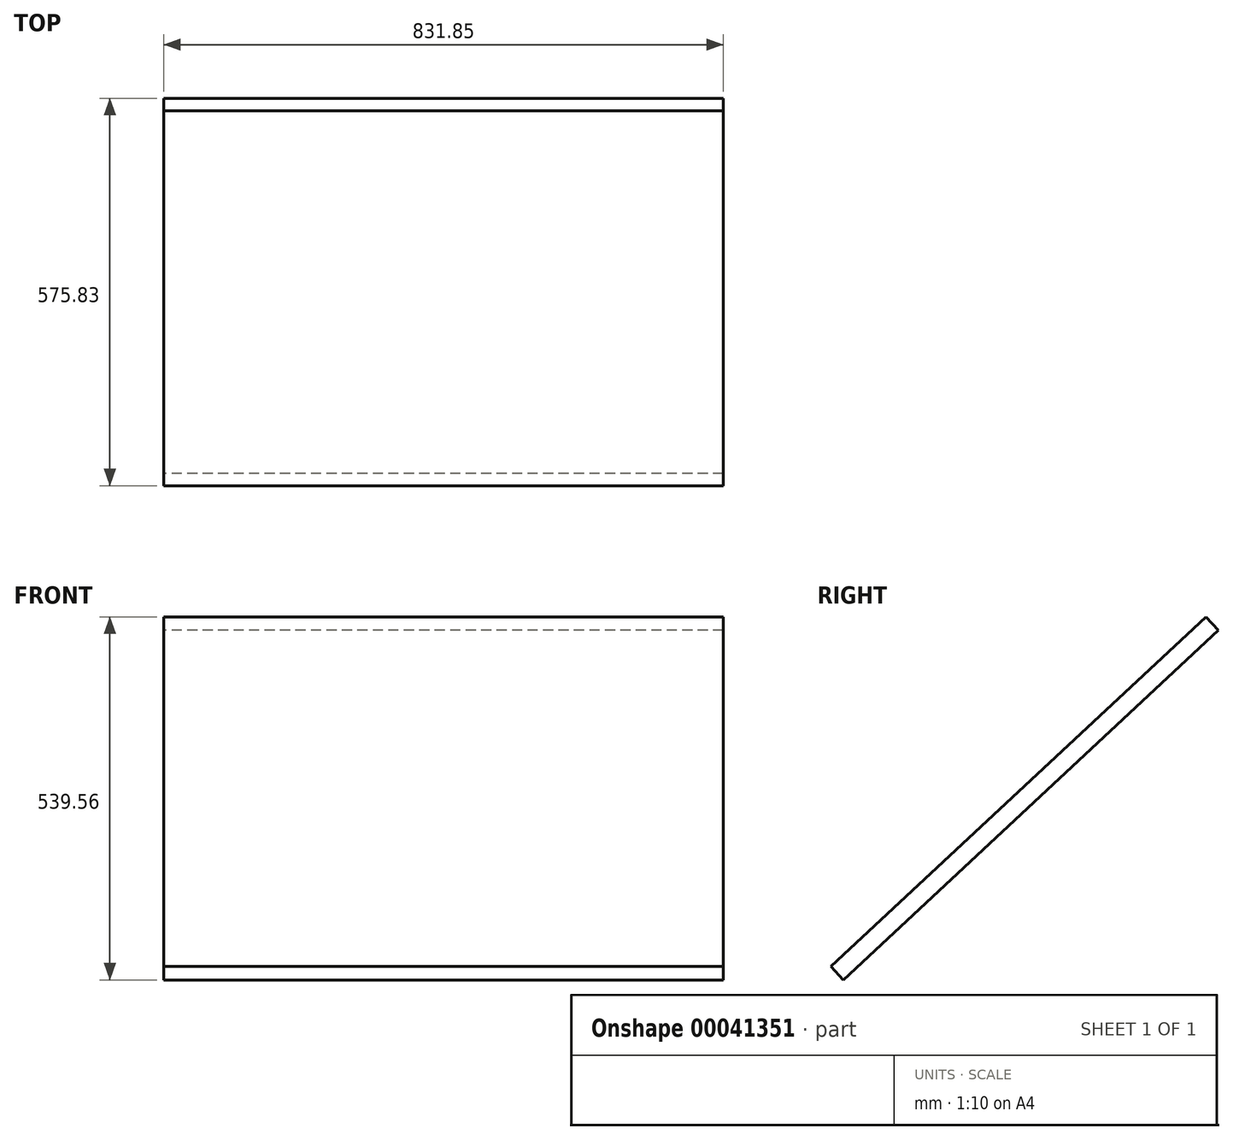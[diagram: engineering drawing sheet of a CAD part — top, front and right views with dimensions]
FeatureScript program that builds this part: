
annotation { "Feature Type Name" : "Feature", "Feature Type Description" : "" }
export const myFeature = defineFeature(function(context is Context, id is Id, definition is map)
    precondition{}
    {
        {
            var Q0;
            Q0=qCreatedBy(makeId("Right.planeOp"),FACE);
            var sketch = newSketch(context, id + "F0", { "sketchPlane" : qUnion([Q0])});
            skLineSegment(sketch, "E0.bottom", {"start": v(0, 713.1) * mm, "end": v(27.18, 713.1) * mm});
            skLineSegment(sketch, "E0.top", {"start": v(0, -48.9) * mm, "end": v(27.18, -48.9) * mm});
            skLineSegment(sketch, "E0.left", {"start": v(0, 713.1) * mm, "end": v(0, -48.9) * mm});
            skLineSegment(sketch, "E0.right", {"start": v(27.18, 713.1) * mm, "end": v(27.18, -48.9) * mm});
            skSolve(sketch);
        }
        {
            var Q0;
            Q0 = qSketchRegion(id + "F0", true);
            extrude(context, id + "F1", {"entities" : qUnion([Q0]), "depth" : 831.85 * mm});
        }
        {
            var Q0;
            Q0=makeQuery(id+"F1.opExtrude","SWEPT_BODY",BODY,{"disambiguationData":[OSD([sQuery(id+"F0.wireOp",EDGE,"E0.bottom"),sQuery(id+"F0.wireOp",EDGE,"E0.top"),sQuery(id+"F0.wireOp",EDGE,"E0.left"),sQuery(id+"F0.wireOp",EDGE,"E0.right")])]});
            var Q1;
            Q1=makeQuery(id+"F1.opExtrude","SWEPT_EDGE",EDGE,{"disambiguationData":[OSD([sQuery(id+"F0.wireOp",EDGE,"E0.top"),sQuery(id+"F0.wireOp",EDGE,"E0.left")])]});
            transform(context, id + "F2", {"entities" : qUnion([Q0]), "transformType" : TransformType.ROTATION, "transformAxis" : qUnion([Q1]), "angle" : 47 * degree, "makeCopy" : false});
        }
    });
